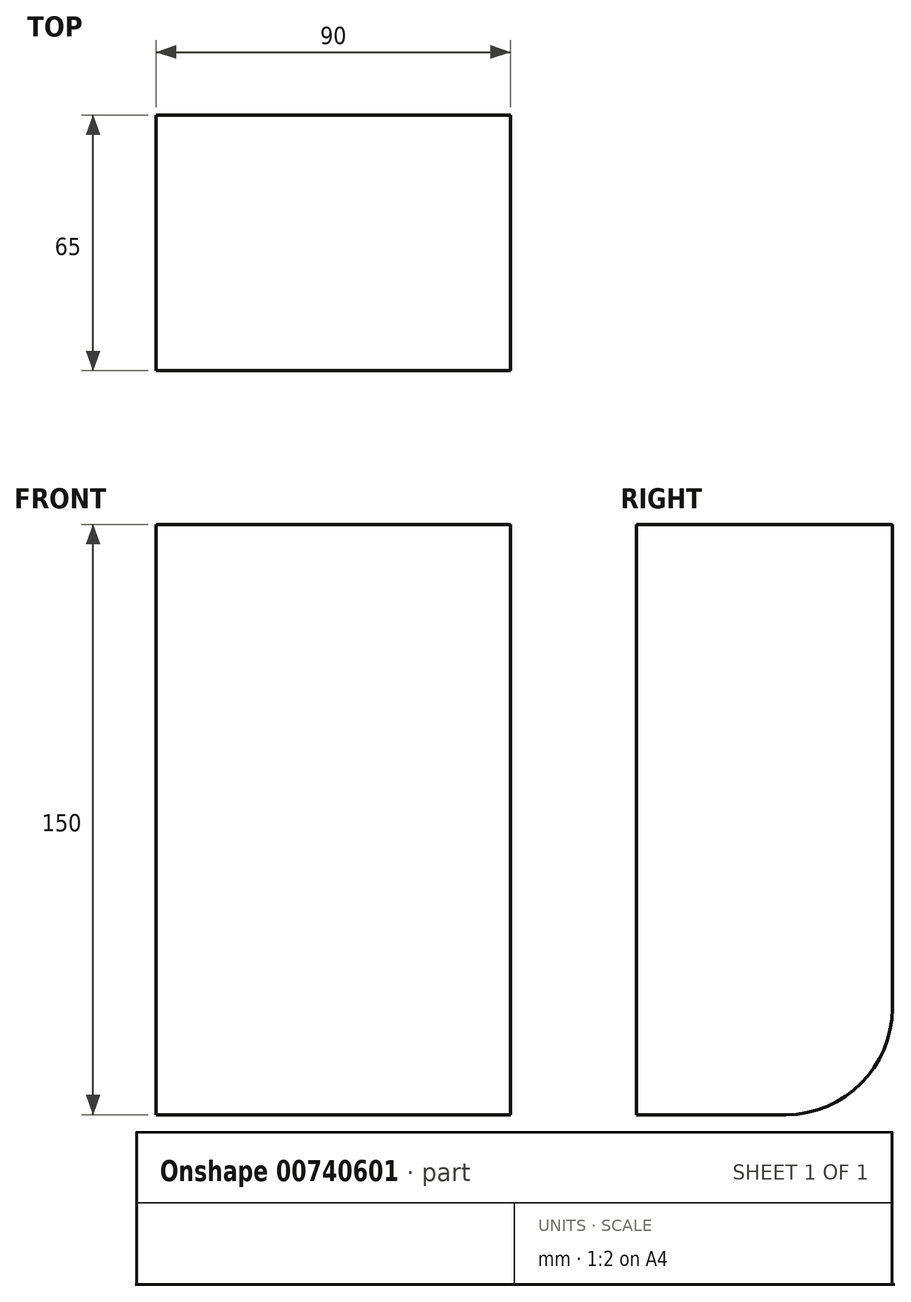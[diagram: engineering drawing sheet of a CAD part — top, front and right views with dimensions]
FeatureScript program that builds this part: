
annotation { "Feature Type Name" : "Feature", "Feature Type Description" : "" }
export const myFeature = defineFeature(function(context is Context, id is Id, definition is map)
    precondition{}
    {
        {
            var Q0;
            Q0=qCreatedBy(makeId("Right.planeOp"),FACE);
            var sketch = newSketch(context, id + "F0", { "sketchPlane" : qUnion([Q0])});
            skLineSegment(sketch, "E0.bottom", {"start": v(-32.5, -75) * mm, "end": v(32.5, -75) * mm});
            skLineSegment(sketch, "E0.top", {"start": v(-32.5, 75) * mm, "end": v(32.5, 75) * mm});
            skLineSegment(sketch, "E0.left", {"start": v(-32.5, -75) * mm, "end": v(-32.5, 75) * mm});
            skLineSegment(sketch, "E0.right", {"start": v(32.5, -75) * mm, "end": v(32.5, 75) * mm});
            skPoint(sketch, "E0.middle", {"position": v(0, 0) * mm});
            skSolve(sketch);
        }
        {
            var Q0;
            Q0=makeQuery(id+"F0.imprint","IMPRINT",FACE,{"disambiguationData":[TD([[makeQuery(id+"F0.imprint","IMPRINT",EDGE,{"derivedFrom":sQuery(id+"F0.wireOp",EDGE,"E0.bottom")}),1.0]])]});
            extrude(context, id + "F1", {"entities" : qUnion([Q0]), "depth" : 90 * mm, "offsetDistance" : 25 * mm});
        }
        {
            var Q0;
            Q0=makeQuery(id+"F1.opExtrude","SWEPT_EDGE",EDGE,{"disambiguationData":[OSD([sQuery(id+"F0.wireOp",EDGE,"E0.bottom"),sQuery(id+"F0.wireOp",EDGE,"E0.right")])]});
            fillet(context, id + "F2", {"entities" : qUnion([Q0]), "radius" : 27 * mm, "tangentPropagation" : true, "allowEdgeOverflow" : false});
        }
    });
